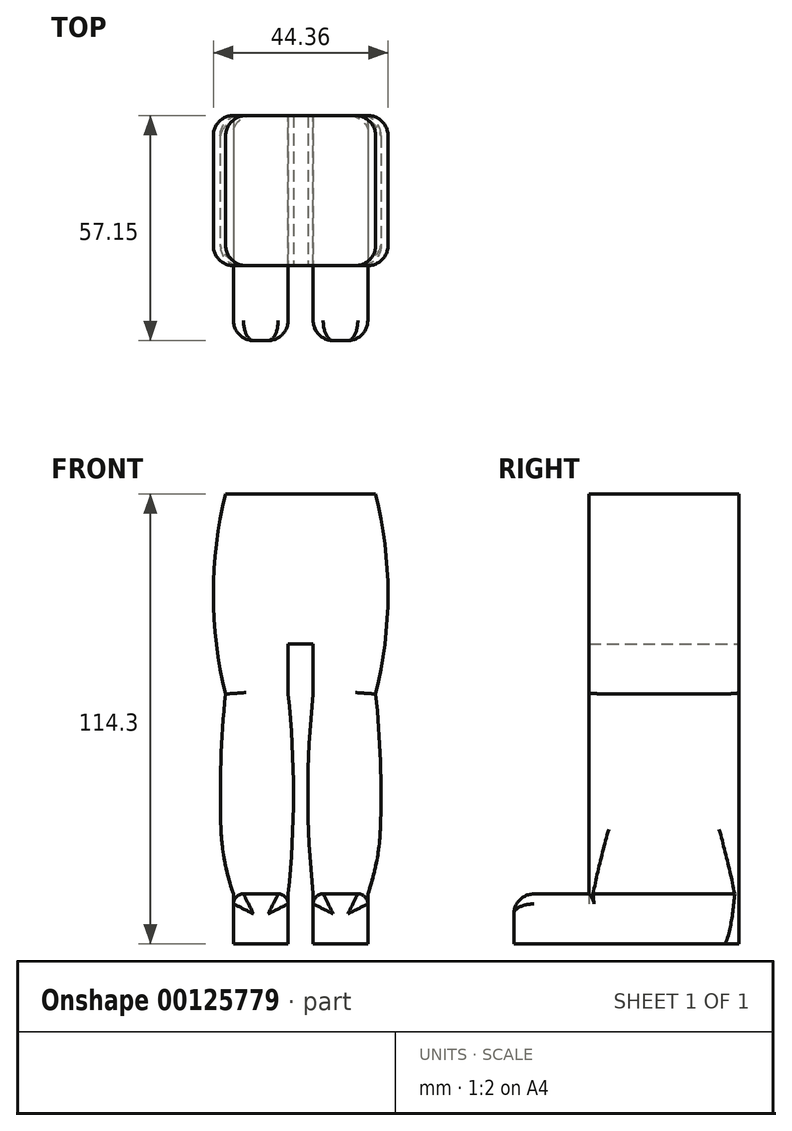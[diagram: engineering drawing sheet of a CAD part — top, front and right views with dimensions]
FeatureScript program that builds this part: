
annotation { "Feature Type Name" : "Feature", "Feature Type Description" : "" }
export const myFeature = defineFeature(function(context is Context, id is Id, definition is map)
    precondition{}
    {
        {
            var Q0;
            Q0=qCreatedBy(makeId("Top.planeOp"),FACE);
            var sketch = newSketch(context, id + "F0", { "sketchPlane" : qUnion([Q0])});
            skLineSegment(sketch, "E0.bottom", {"start": v(19.05, 19.05) * mm, "end": v(-19.05, 19.05) * mm});
            skLineSegment(sketch, "E0.top", {"start": v(19.05, -19.05) * mm, "end": v(-19.05, -19.05) * mm});
            skLineSegment(sketch, "E0.left", {"start": v(19.05, 19.05) * mm, "end": v(19.05, -19.05) * mm});
            skLineSegment(sketch, "E0.right", {"start": v(-19.05, 19.05) * mm, "end": v(-19.05, -19.05) * mm});
            skPoint(sketch, "E0.middle", {"position": v(0, 0) * mm});
            skSolve(sketch);
        }
        {
            var Q0;
            Q0 = qSketchRegion(id + "F0", true);
            extrude(context, id + "F1", {"entities" : qUnion([Q0]), "oppositeDirection" : true, "depth" : 101.6 * mm});
        }
        {
            var Q0;
            Q0=makeQuery(id+"F1.opExtrude","SWEPT_FACE",FACE,{"disambiguationData":[OSD([sQuery(id+"F0.wireOp",EDGE,"E0.top")])]});
            var sketch = newSketch(context, id + "F2", { "sketchPlane" : qUnion([Q0])});
            skArc(sketch, "E1", {"start": v(19.05, -50.8) * mm, "mid": v(22.18, -25.4) * mm, "end": v(19.05, 0) * mm});
            skLineSegment(sketch, "E2", {"start": v(0, 0) * mm, "end": v(0, -57.52) * mm, "construction": true});
            skPoint(sketch, "E2.endSnap0", {"position": v(0, 0) * mm});
            skLineSegment(sketch, "E3", {"start": v(19.05, 0) * mm, "end": v(19.05, -50.8) * mm});
            skArc(sketch, "E4.MirrorCS", {"start": v(-19.05, -50.8) * mm, "mid": v(-22.18, -25.4) * mm, "end": v(-19.05, 0) * mm});
            skLineSegment(sketch, "E5.MirrorCS", {"start": v(-19.05, 0) * mm, "end": v(-19.05, -50.8) * mm});
            skSolve(sketch);
        }
        {
            var Q0;
            Q0 = qSketchRegion(id + "F2", true);
            extrude(context, id + "F3", {"entities" : qUnion([Q0]), "operationType" : NewBodyOperationType.ADD, "oppositeDirection" : true, "depth" : 38.1 * mm});
        }
        {
            var Q0;
            Q0=makeQuery(id+"F1.opExtrude","CAP_FACE",FACE,{"disambiguationData":[OSD([sQuery(id+"F0.wireOp",EDGE,"E0.bottom"),sQuery(id+"F0.wireOp",EDGE,"E0.top"),sQuery(id+"F0.wireOp",EDGE,"E0.left"),sQuery(id+"F0.wireOp",EDGE,"E0.right")])],"isStart":false});
            var sketch = newSketch(context, id + "F4", { "sketchPlane" : qUnion([Q0])});
            skPoint(sketch, "E6", {"position": v(0, 19.05) * mm});
            skLineSegment(sketch, "E7.bottom", {"start": v(-3.18, 19.05) * mm, "end": v(3.18, 19.05) * mm});
            skLineSegment(sketch, "E7.top", {"start": v(-3.18, -19.05) * mm, "end": v(3.18, -19.05) * mm});
            skLineSegment(sketch, "E7.left", {"start": v(-3.18, 19.05) * mm, "end": v(-3.18, -19.05) * mm});
            skLineSegment(sketch, "E7.right", {"start": v(3.18, 19.05) * mm, "end": v(3.18, -19.05) * mm});
            skSolve(sketch);
        }
        {
            var Q0;
            Q0 = qSketchRegion(id + "F4", true);
            extrude(context, id + "F5", {"entities" : qUnion([Q0]), "operationType" : NewBodyOperationType.REMOVE, "oppositeDirection" : true, "depth" : 63.5 * mm});
        }
        {
            var Q0;
            Q0=makeQuery(id+"F3.boolean.opBoolean","MERGE",FACE,{"derivedFrom":[makeQuery(id+"F1.opExtrude","SWEPT_FACE",FACE,{"disambiguationData":[OSD([sQuery(id+"F0.wireOp",EDGE,"E0.top")])]}),makeQuery(id+"F3.opExtrude","CAP_FACE",FACE,{"disambiguationData":[OSD([sQuery(id+"F2.wireOp",EDGE,"E1"),sQuery(id+"F2.wireOp",EDGE,"E3")])],"isStart":true}),makeQuery(id+"F3.opExtrude","CAP_FACE",FACE,{"disambiguationData":[OSD([sQuery(id+"F2.wireOp",EDGE,"E4.MirrorCS"),sQuery(id+"F2.wireOp",EDGE,"E5.MirrorCS")])],"isStart":true})]});
            var sketch = newSketch(context, id + "F6", { "sketchPlane" : qUnion([Q0])});
            skArc(sketch, "E8", {"start": v(19.05, -101.6) * mm, "mid": v(20.41, -76.2) * mm, "end": v(19.05, -50.8) * mm});
            skLineSegment(sketch, "E9", {"start": v(0, 0) * mm, "end": v(0, -101.6) * mm, "construction": true});
            skLineSegment(sketch, "E10", {"start": v(19.05, -50.8) * mm, "end": v(19.05, -101.6) * mm});
            skLineSegment(sketch, "E11", {"start": v(11.11, -101.6) * mm, "end": v(11.11, -43.02) * mm, "construction": true});
            skLineSegment(sketch, "E12.MirrorCS", {"start": v(3.18, -50.8) * mm, "end": v(3.18, -101.6) * mm});
            skArc(sketch, "E13.MirrorCS", {"start": v(3.18, -101.6) * mm, "mid": v(1.81, -76.2) * mm, "end": v(3.18, -50.8) * mm});
            skLineSegment(sketch, "E14.MirrorCS", {"start": v(-3.18, -50.8) * mm, "end": v(-3.18, -101.6) * mm});
            skArc(sketch, "E15.MirrorCS", {"start": v(-3.18, -101.6) * mm, "mid": v(-1.81, -76.2) * mm, "end": v(-3.18, -50.8) * mm});
            skLineSegment(sketch, "E16.MirrorCS", {"start": v(-19.05, -50.8) * mm, "end": v(-19.05, -101.6) * mm});
            skArc(sketch, "E17.MirrorCS", {"start": v(-19.05, -101.6) * mm, "mid": v(-20.41, -76.2) * mm, "end": v(-19.05, -50.8) * mm});
            skSolve(sketch);
        }
        {
            var Q0;
            Q0 = qSketchRegion(id + "F6", true);
            extrude(context, id + "F7", {"entities" : qUnion([Q0]), "operationType" : NewBodyOperationType.ADD, "oppositeDirection" : true, "depth" : 38.1 * mm});
        }
        {
            var Q0;
            Q0=makeQuery(id+"F7.boolean.opBoolean","MERGE",FACE,{"derivedFrom":[makeQuery(id+"F3.boolean.opBoolean","MERGE",FACE,{"derivedFrom":[makeQuery(id+"F1.opExtrude","SWEPT_FACE",FACE,{"disambiguationData":[OSD([sQuery(id+"F0.wireOp",EDGE,"E0.top")])]}),makeQuery(id+"F3.opExtrude","CAP_FACE",FACE,{"disambiguationData":[OSD([sQuery(id+"F2.wireOp",EDGE,"E1"),sQuery(id+"F2.wireOp",EDGE,"E3")])],"isStart":true}),makeQuery(id+"F3.opExtrude","CAP_FACE",FACE,{"disambiguationData":[OSD([sQuery(id+"F2.wireOp",EDGE,"E4.MirrorCS"),sQuery(id+"F2.wireOp",EDGE,"E5.MirrorCS")])],"isStart":true})]}),makeQuery(id+"F7.opExtrude","CAP_FACE",FACE,{"disambiguationData":[OSD([sQuery(id+"F6.wireOp",EDGE,"E8"),sQuery(id+"F6.wireOp",EDGE,"E10")])],"isStart":true}),makeQuery(id+"F7.opExtrude","CAP_FACE",FACE,{"disambiguationData":[OSD([sQuery(id+"F6.wireOp",EDGE,"E12.MirrorCS"),sQuery(id+"F6.wireOp",EDGE,"E13.MirrorCS")])],"isStart":true}),makeQuery(id+"F7.opExtrude","CAP_FACE",FACE,{"disambiguationData":[OSD([sQuery(id+"F6.wireOp",EDGE,"E14.MirrorCS"),sQuery(id+"F6.wireOp",EDGE,"E15.MirrorCS")])],"isStart":true}),makeQuery(id+"F7.opExtrude","CAP_FACE",FACE,{"disambiguationData":[OSD([sQuery(id+"F6.wireOp",EDGE,"E16.MirrorCS"),sQuery(id+"F6.wireOp",EDGE,"E17.MirrorCS")])],"isStart":true})]});
            var sketch = newSketch(context, id + "F8", { "sketchPlane" : qUnion([Q0])});
            skPoint(sketch, "E18", {"position": v(11.11, -101.6) * mm});
            skPoint(sketch, "E19", {"position": v(-11.11, -101.6) * mm});
            skArc(sketch, "E20", {"start": v(17.06, -101.6) * mm, "mid": v(19.34, -93.13) * mm, "end": v(20.27, -84.42) * mm});
            skLineSegment(sketch, "E21", {"start": v(11.11, -101.6) * mm, "end": v(11.11, -80.58) * mm, "construction": true});
            skArc(sketch, "E22.MirrorCS", {"start": v(5.16, -101.6) * mm, "mid": v(2.9, -93.13) * mm, "end": v(1.96, -84.42) * mm});
            skPoint(sketch, "E23", {"position": v(0, -101.6) * mm});
            skLineSegment(sketch, "E24", {"start": v(0, -101.6) * mm, "end": v(0, -41.42) * mm, "construction": true});
            skArc(sketch, "E25.MirrorCS", {"start": v(-5.16, -101.6) * mm, "mid": v(-2.9, -93.13) * mm, "end": v(-1.96, -84.42) * mm});
            skArc(sketch, "E26.MirrorCS", {"start": v(-17.06, -101.6) * mm, "mid": v(-19.34, -93.13) * mm, "end": v(-20.27, -84.42) * mm});
            skLineSegment(sketch, "E27", {"start": v(20.27, -84.42) * mm, "end": v(22.36, -103.23) * mm});
            skLineSegment(sketch, "E28", {"start": v(22.36, -103.23) * mm, "end": v(17.06, -101.6) * mm});
            skLineSegment(sketch, "E29", {"start": v(-20.27, -84.42) * mm, "end": v(-23.8, -102.8) * mm});
            skLineSegment(sketch, "E30", {"start": v(-23.8, -102.8) * mm, "end": v(-17.06, -101.6) * mm});
            skSolve(sketch);
        }
        {
            var Q0;
            Q0 = qSketchRegion(id + "F8", true);
            extrude(context, id + "F9", {"entities" : qUnion([Q0]), "operationType" : NewBodyOperationType.REMOVE, "oppositeDirection" : true, "depth" : 38.1 * mm});
        }
        {
            var Q0;
            {var subQ0=sQuery(id+"F0.wireOp",EDGE,"E0.left");var subQ3=sQuery(id+"F0.wireOp",EDGE,"E0.top");var subQ4=sQuery(id+"F0.wireOp",EDGE,"E0.bottom");Q0=makeQuery(id+"F5.boolean.opBoolean","SPLIT",FACE,{"disambiguationData":[TD([makeQuery(id+"F1.opExtrude","SWEPT_FACE",FACE,{"disambiguationData":[OSD([subQ0])]})])],"derivedFrom":makeQuery(id+"F1.opExtrude","CAP_FACE",FACE,{"disambiguationData":[OSD([subQ4,subQ3,subQ0,sQuery(id+"F0.wireOp",EDGE,"E0.right")])],"isStart":false})});}
            var sketch = newSketch(context, id + "F10", { "sketchPlane" : qUnion([Q0])});
            skLineSegment(sketch, "E31.0.0", {"start": v(17.06, -19.05) * mm, "end": v(17.06, 38.1) * mm});
            skLineSegment(sketch, "E31.0.1", {"start": v(17.06, 38.1) * mm, "end": v(3.18, 38.1) * mm});
            skLineSegment(sketch, "E31.0.2", {"start": v(3.18, 38.1) * mm, "end": v(3.18, -19.05) * mm});
            skLineSegment(sketch, "E31.0.3", {"start": v(3.18, -19.05) * mm, "end": v(17.06, -19.05) * mm});
            skLineSegment(sketch, "E32", {"start": v(0, 0) * mm, "end": v(0, 59.88) * mm, "construction": true});
            skLineSegment(sketch, "E33.MirrorCS", {"start": v(-3.18, 38.1) * mm, "end": v(-3.18, -19.05) * mm});
            skLineSegment(sketch, "E34.MirrorCS", {"start": v(-17.06, -19.05) * mm, "end": v(-17.06, 38.1) * mm});
            skLineSegment(sketch, "E35.MirrorCS", {"start": v(-17.06, 38.1) * mm, "end": v(-3.18, 38.1) * mm});
            skLineSegment(sketch, "E36.MirrorCS", {"start": v(-3.18, -19.05) * mm, "end": v(-17.06, -19.05) * mm});
            skSolve(sketch);
        }
        {
            var Q0;
            Q0 = qSketchRegion(id + "F10", true);
            extrude(context, id + "F11", {"entities" : qUnion([Q0]), "operationType" : NewBodyOperationType.ADD, "depth" : 12.7 * mm});
        }
        {
            var Q0;
            Q0=makeQuery(id+"F11.boolean.opBoolean","SPLIT",EDGE,{"derivedFrom":makeQuery(id+"F11.opExtrude","CAP_EDGE",EDGE,{"disambiguationData":[OSD([sQuery(id+"F10.wireOp",EDGE,"E31.0.0")])],"isStart":true})});
            var Q1;
            Q1=makeQuery(id+"F11.boolean.opBoolean","SPLIT",EDGE,{"derivedFrom":makeQuery(id+"F11.opExtrude","CAP_EDGE",EDGE,{"disambiguationData":[OSD([sQuery(id+"F10.wireOp",EDGE,"E31.0.2")])],"isStart":true})});
            var Q2;
            Q2=makeQuery(id+"F11.boolean.opBoolean","SPLIT",EDGE,{"derivedFrom":makeQuery(id+"F11.opExtrude","CAP_EDGE",EDGE,{"disambiguationData":[OSD([sQuery(id+"F10.wireOp",EDGE,"E33.MirrorCS")])],"isStart":true})});
            var Q3;
            Q3=makeQuery(id+"F11.boolean.opBoolean","SPLIT",EDGE,{"derivedFrom":makeQuery(id+"F11.opExtrude","CAP_EDGE",EDGE,{"disambiguationData":[OSD([sQuery(id+"F10.wireOp",EDGE,"E34.MirrorCS")])],"isStart":true})});
            fillet(context, id + "F12", {"entities" : qUnion([Q0, Q1, Q2, Q3]), "radius" : 2.54 * mm, "tangentPropagation" : true, "allowEdgeOverflow" : false});
        }
        {
            var Q0;
            Q0=makeQuery(id+"F11.opExtrude","CAP_EDGE",EDGE,{"disambiguationData":[OSD([sQuery(id+"F10.wireOp",EDGE,"E31.0.1")])],"isStart":true});
            var Q1;
            Q1=makeQuery(id+"F11.opExtrude","CAP_EDGE",EDGE,{"disambiguationData":[OSD([sQuery(id+"F10.wireOp",EDGE,"E35.MirrorCS")])],"isStart":true});
            fillet(context, id + "F13", {"entities" : qUnion([Q0, Q1]), "radius" : 5.08 * mm, "tangentPropagation" : true, "allowEdgeOverflow" : false});
        }
        {
            var Q0;
            Q0=makeQuery(id+"F3.opExtrude","CAP_EDGE",EDGE,{"disambiguationData":[OSD([sQuery(id+"F2.wireOp",EDGE,"E1")])],"isStart":false});
            var Q1;
            Q1=makeQuery(id+"F3.opExtrude","CAP_EDGE",EDGE,{"disambiguationData":[OSD([sQuery(id+"F2.wireOp",EDGE,"E4.MirrorCS")])],"isStart":false});
            var Q2;
            Q2=makeQuery(id+"F7.opExtrude","CAP_EDGE",EDGE,{"disambiguationData":[OSD([sQuery(id+"F6.wireOp",EDGE,"E8")])],"isStart":false});
            var Q3;
            Q3=makeQuery(id+"F7.opExtrude","CAP_EDGE",EDGE,{"disambiguationData":[OSD([sQuery(id+"F6.wireOp",EDGE,"E17.MirrorCS")])],"isStart":false});
            var Q4;
            Q4=makeQuery(id+"F7.opExtrude","CAP_EDGE",EDGE,{"disambiguationData":[OSD([sQuery(id+"F6.wireOp",EDGE,"E17.MirrorCS")])],"isStart":true});
            var Q5;
            Q5=makeQuery(id+"F9.boolean.opBoolean","COPY",EDGE,{"derivedFrom":makeQuery(id+"F9.opExtrude","CAP_EDGE",EDGE,{"disambiguationData":[OSD([sQuery(id+"F8.wireOp",EDGE,"E26.MirrorCS")])],"isStart":true})});
            var Q6;
            Q6=makeQuery(id+"F3.opExtrude","CAP_EDGE",EDGE,{"disambiguationData":[OSD([sQuery(id+"F2.wireOp",EDGE,"E4.MirrorCS")])],"isStart":true});
            var Q7;
            Q7=makeQuery(id+"F3.opExtrude","CAP_EDGE",EDGE,{"disambiguationData":[OSD([sQuery(id+"F2.wireOp",EDGE,"E1")])],"isStart":true});
            var Q8;
            Q8=makeQuery(id+"F7.opExtrude","CAP_EDGE",EDGE,{"disambiguationData":[OSD([sQuery(id+"F6.wireOp",EDGE,"E8")])],"isStart":true});
            fillet(context, id + "F14", {"entities" : qUnion([Q0, Q1, Q2, Q3, Q4, Q5, Q6, Q7, Q8]), "radius" : 5.08 * mm, "tangentPropagation" : true, "allowEdgeOverflow" : false});
        }
    });
